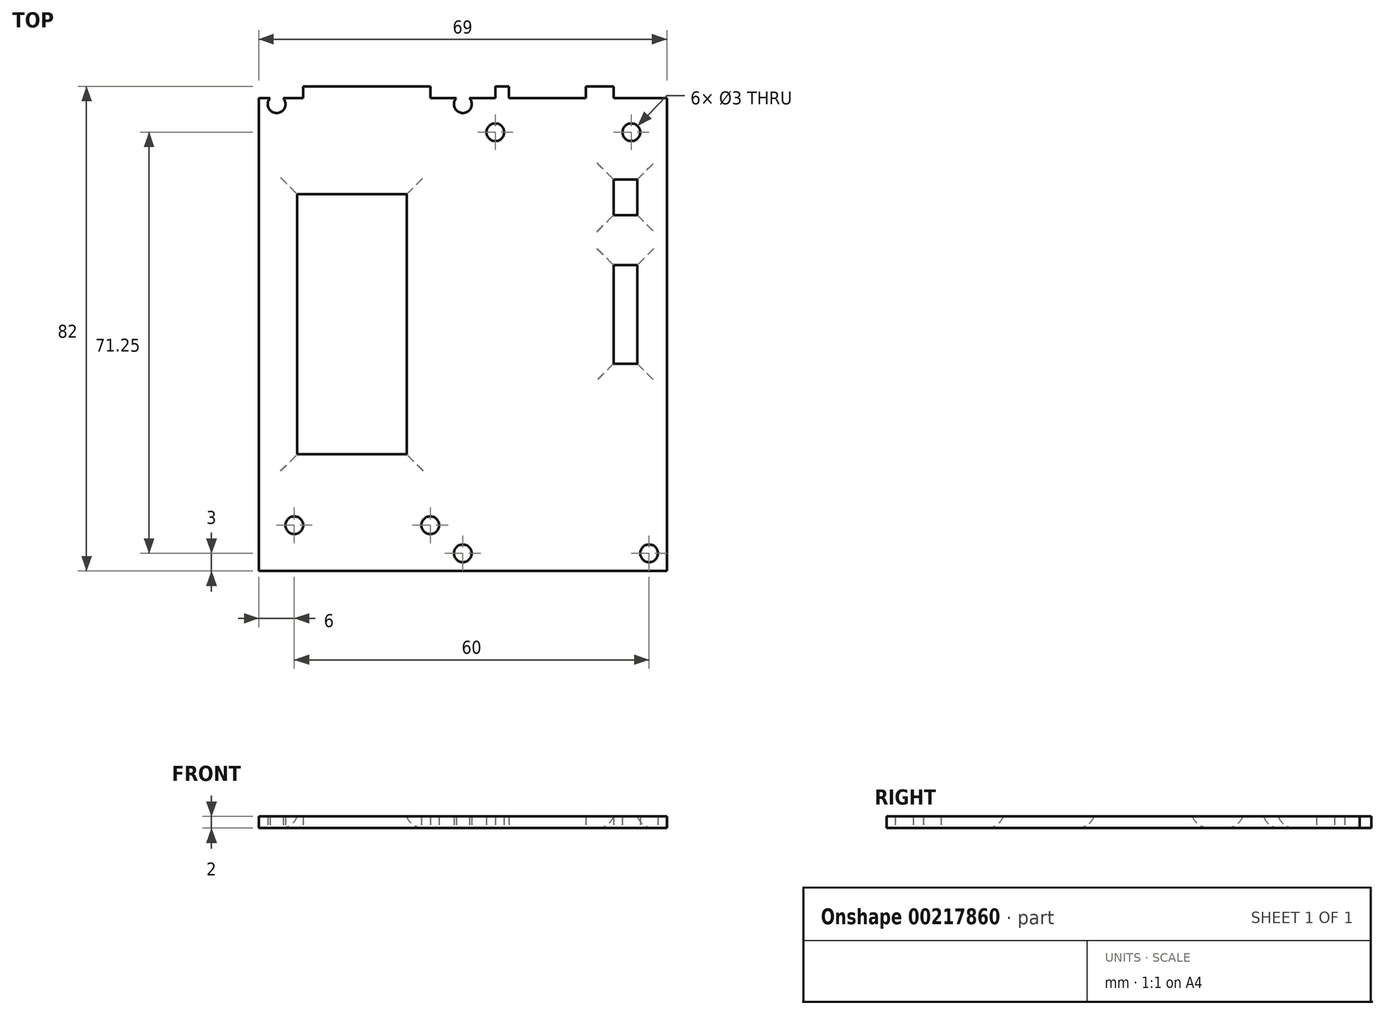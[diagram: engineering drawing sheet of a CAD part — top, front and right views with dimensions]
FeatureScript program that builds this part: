
annotation { "Feature Type Name" : "Feature", "Feature Type Description" : "" }
export const myFeature = defineFeature(function(context is Context, id is Id, definition is map)
    precondition{}
    {
        {
            var Q0;
            Q0=qCreatedBy(makeId("Top.planeOp"),FACE);
            var sketch = newSketch(context, id + "F0", { "sketchPlane" : qUnion([Q0])});
            skLineSegment(sketch, "E0.bottom", {"start": v(34.5, -41) * mm, "end": v(-34.5, -41) * mm});
            skLineSegment(sketch, "E0.top", {"start": v(34.5, 41) * mm, "end": v(-34.5, 41) * mm});
            skLineSegment(sketch, "E0.left", {"start": v(34.5, -41) * mm, "end": v(34.5, 41) * mm});
            skLineSegment(sketch, "E0.right", {"start": v(-34.5, -41) * mm, "end": v(-34.5, 41) * mm});
            skPoint(sketch, "E0.middle", {"position": v(0, 0) * mm});
            skLineSegment(sketch, "E1", {"start": v(-34.5, 39) * mm, "end": v(34.5, 39) * mm});
            skCircle(sketch, "E2.MirrorC", {"center": v(31.5, -38) * mm, "radius": 1.5 * mm});
            skCircle(sketch, "E3", {"center": v(0, -38) * mm, "radius": 1.5 * mm});
            skCircle(sketch, "E4", {"center": v(-28.5, 33.25) * mm, "radius": 1.5 * mm});
            skCircle(sketch, "E5", {"center": v(-5.5, 33.25) * mm, "radius": 1.5 * mm});
            skCircle(sketch, "E6.MirrorC", {"center": v(5.5, 33.25) * mm, "radius": 1.5 * mm});
            skCircle(sketch, "E7.MirrorC", {"center": v(28.5, 33.25) * mm, "radius": 1.5 * mm});
            skLineSegment(sketch, "E8.bottom", {"start": v(-28, 22.75) * mm, "end": v(-9.5, 22.75) * mm});
            skLineSegment(sketch, "E8.top", {"start": v(-28, -21.25) * mm, "end": v(-9.5, -21.25) * mm});
            skLineSegment(sketch, "E8.left", {"start": v(-28, 22.75) * mm, "end": v(-28, -21.25) * mm});
            skLineSegment(sketch, "E8.right", {"start": v(-9.5, 22.75) * mm, "end": v(-9.5, -21.25) * mm});
            skLineSegment(sketch, "E9.bottom", {"start": v(25.5, 25.25) * mm, "end": v(29.5, 25.25) * mm});
            skLineSegment(sketch, "E9.top", {"start": v(25.5, 19.25) * mm, "end": v(29.5, 19.25) * mm});
            skLineSegment(sketch, "E9.left", {"start": v(25.5, 25.25) * mm, "end": v(25.5, 19.25) * mm});
            skLineSegment(sketch, "E9.right", {"start": v(29.5, 25.25) * mm, "end": v(29.5, 19.25) * mm});
            skLineSegment(sketch, "E10.bottom", {"start": v(29.5, 10.75) * mm, "end": v(25.5, 10.75) * mm});
            skLineSegment(sketch, "E10.top", {"start": v(29.5, -5.91) * mm, "end": v(25.5, -5.91) * mm});
            skLineSegment(sketch, "E10.left", {"start": v(29.5, 10.75) * mm, "end": v(29.5, -5.91) * mm});
            skLineSegment(sketch, "E10.right", {"start": v(25.5, 10.75) * mm, "end": v(25.5, -5.91) * mm});
            skLineSegment(sketch, "E11.bottom", {"start": v(-5.5, 41) * mm, "end": v(5.5, 41) * mm});
            skLineSegment(sketch, "E11.top", {"start": v(-5.5, 39) * mm, "end": v(5.5, 39) * mm});
            skLineSegment(sketch, "E11.left", {"start": v(-5.5, 41) * mm, "end": v(-5.5, 39) * mm});
            skLineSegment(sketch, "E11.right", {"start": v(5.5, 41) * mm, "end": v(5.5, 39) * mm});
            skLineSegment(sketch, "E12.bottom", {"start": v(28.5, 39) * mm, "end": v(34.5, 39) * mm});
            skLineSegment(sketch, "E12.top", {"start": v(28, 41) * mm, "end": v(34.5, 41) * mm});
            skLineSegment(sketch, "E12.right", {"start": v(34.5, 39) * mm, "end": v(34.5, 41) * mm});
            skLineSegment(sketch, "E13.bottom", {"start": v(-28.5, 39) * mm, "end": v(-34.5, 39) * mm});
            skLineSegment(sketch, "E13.top", {"start": v(-27, 41) * mm, "end": v(-34.5, 41) * mm});
            skLineSegment(sketch, "E13.right", {"start": v(-34.5, 39) * mm, "end": v(-34.5, 41) * mm});
            skLineSegment(sketch, "E14", {"start": v(-25.5, 41) * mm, "end": v(-25.5, 39) * mm});
            skLineSegment(sketch, "E15.MirrorCS", {"start": v(25.5, 41) * mm, "end": v(25.5, 39) * mm});
            skLineSegment(sketch, "E16.bottom", {"start": v(-37, 41) * mm, "end": v(37, 41) * mm});
            skLineSegment(sketch, "E16.top", {"start": v(-37, -43.29) * mm, "end": v(37, -43.29) * mm});
            skLineSegment(sketch, "E16.left", {"start": v(-37, 41) * mm, "end": v(-37, -43.29) * mm});
            skLineSegment(sketch, "E16.right", {"start": v(37, 41) * mm, "end": v(37, -43.29) * mm});
            skLineSegment(sketch, "E17.bottom", {"start": v(-10.5, -43.29) * mm, "end": v(10.5, -43.29) * mm});
            skLineSegment(sketch, "E17.top", {"start": v(-10.5, -51.29) * mm, "end": v(10.5, -51.29) * mm});
            skLineSegment(sketch, "E17.left", {"start": v(-10.5, -43.29) * mm, "end": v(-10.5, -51.29) * mm});
            skLineSegment(sketch, "E17.right", {"start": v(10.5, -43.29) * mm, "end": v(10.5, -51.29) * mm});
            skLineSegment(sketch, "E18.bottom", {"start": v(-12.5, -41) * mm, "end": v(12.5, -41) * mm});
            skLineSegment(sketch, "E18.top", {"start": v(-12.5, -53.5) * mm, "end": v(12.5, -53.5) * mm});
            skLineSegment(sketch, "E18.left", {"start": v(-12.5, -41) * mm, "end": v(-12.5, -53.5) * mm});
            skLineSegment(sketch, "E18.right", {"start": v(12.5, -41) * mm, "end": v(12.5, -53.5) * mm});
            skLineSegment(sketch, "E19", {"start": v(-10.5, -43.29) * mm, "end": v(-10.5, -41) * mm});
            skLineSegment(sketch, "E20.MirrorCS", {"start": v(10.5, -43.29) * mm, "end": v(10.5, -41) * mm});
            skLineSegment(sketch, "E21.bottom", {"start": v(20.8, 41) * mm, "end": v(7.8, 41) * mm});
            skLineSegment(sketch, "E21.top", {"start": v(20.8, 39) * mm, "end": v(7.8, 39) * mm});
            skLineSegment(sketch, "E21.left", {"start": v(20.8, 41) * mm, "end": v(20.8, 39) * mm});
            skLineSegment(sketch, "E21.right", {"start": v(7.8, 41) * mm, "end": v(7.8, 39) * mm});
            skLineSegment(sketch, "E22", {"start": v(-14.5, 41) * mm, "end": v(-14.5, 39) * mm});
            skLineSegment(sketch, "E23", {"start": v(-27, 41) * mm, "end": v(-27, 39) * mm});
            skLineSegment(sketch, "E24.top", {"start": v(-37, 43) * mm, "end": v(37, 43) * mm});
            skLineSegment(sketch, "E24.left", {"start": v(-37, 41) * mm, "end": v(-37, 43) * mm});
            skLineSegment(sketch, "E24.right", {"start": v(37, 41) * mm, "end": v(37, 43) * mm});
            skCircle(sketch, "E25.MirrorC", {"center": v(-31.5, 38) * mm, "radius": 1.5 * mm});
            skCircle(sketch, "E26", {"center": v(-28.5, -33.25) * mm, "radius": 1.5 * mm});
            skCircle(sketch, "E27", {"center": v(-5.5, -33.25) * mm, "radius": 1.5 * mm});
            skCircle(sketch, "E28.MirrorC", {"center": v(0, 38) * mm, "radius": 1.5 * mm});
            skSolve(sketch);
        }
        {
            var Q0;
            {var subQ2=sQuery(id+"F0.wireOp",EDGE,"E0.bottom");Q0=makeQuery(id+"F0.imprint","IMPRINT",FACE,{"disambiguationData":[TD([[makeQuery(id+"F0.imprint","IMPRINT",EDGE,{"derivedFrom":subQ2}),-1.0]])]});}
            var Q1;
            {var subQ2=sQuery(id+"F0.wireOp",EDGE,"E13.bottom");Q1=makeQuery(id+"F0.imprint","IMPRINT",FACE,{"disambiguationData":[TD([[makeQuery(id+"F0.imprint","IMPRINT",EDGE,{"derivedFrom":subQ2}),-1.0]])]});}
            var Q2;
            {var subQ0=sQuery(id+"F0.wireOp",EDGE,"E14");Q2=makeQuery(id+"F0.imprint","IMPRINT",FACE,{"disambiguationData":[TD([[makeQuery(id+"F0.imprint","IMPRINT",EDGE,{"derivedFrom":subQ0}),-1.0]])]});}
            var Q3;
            {var subQ0=sQuery(id+"F0.wireOp",EDGE,"E14");Q3=makeQuery(id+"F0.imprint","IMPRINT",FACE,{"disambiguationData":[TD([[makeQuery(id+"F0.imprint","IMPRINT",EDGE,{"derivedFrom":subQ0}),1.0]])]});}
            var Q4;
            {var subQ0=sQuery(id+"F0.wireOp",EDGE,"E11.left");Q4=makeQuery(id+"F0.imprint","IMPRINT",FACE,{"disambiguationData":[TD([[makeQuery(id+"F0.imprint","IMPRINT",EDGE,{"derivedFrom":subQ0}),-1.0]])]});}
            var Q5;
            Q5=makeQuery(id+"F0.imprint","IMPRINT",FACE,{"disambiguationData":[TD([[makeQuery(id+"F0.imprint","IMPRINT",EDGE,{"derivedFrom":sQuery(id+"F0.wireOp",EDGE,"E11.top")}),1.0]])]});
            var Q6;
            {var subQ0=sQuery(id+"F0.wireOp",EDGE,"E11.right");Q6=makeQuery(id+"F0.imprint","IMPRINT",FACE,{"disambiguationData":[TD([[makeQuery(id+"F0.imprint","IMPRINT",EDGE,{"derivedFrom":subQ0}),1.0]])]});}
            var Q7;
            Q7=makeQuery(id+"F0.imprint","IMPRINT",FACE,{"disambiguationData":[TD([[makeQuery(id+"F0.imprint","IMPRINT",EDGE,{"derivedFrom":sQuery(id+"F0.wireOp",EDGE,"E21.top")}),-1.0]])]});
            var Q8;
            {var subQ0=sQuery(id+"F0.wireOp",EDGE,"E15.MirrorCS");Q8=makeQuery(id+"F0.imprint","IMPRINT",FACE,{"disambiguationData":[TD([[makeQuery(id+"F0.imprint","IMPRINT",EDGE,{"derivedFrom":subQ0}),-1.0]])]});}
            var Q9;
            {var subQ2=sQuery(id+"F0.wireOp",EDGE,"E12.bottom");Q9=makeQuery(id+"F0.imprint","IMPRINT",FACE,{"disambiguationData":[TD([[makeQuery(id+"F0.imprint","IMPRINT",EDGE,{"derivedFrom":subQ2}),1.0]])]});}
            var Q10;
            Q10=makeQuery(id+"F0.imprint","IMPRINT",FACE,{"disambiguationData":[TD([[makeQuery(id+"F0.imprint","IMPRINT",EDGE,{"derivedFrom":sQuery(id+"F0.wireOp",EDGE,"E5")}),1.0]])]});
            var Q11;
            Q11=makeQuery(id+"F0.imprint","IMPRINT",FACE,{"disambiguationData":[TD([[makeQuery(id+"F0.imprint","IMPRINT",EDGE,{"derivedFrom":sQuery(id+"F0.wireOp",EDGE,"E4")}),1.0]])]});
            extrude(context, id + "F1", {"entities" : qUnion([Q0, Q1, Q2, Q3, Q4, Q5, Q6, Q7, Q8, Q9, Q10, Q11]), "depth" : 2 * mm});
        }
        {
            var Q0;
            Q0=makeQuery(id+"F1.opExtrude","CAP_EDGE",EDGE,{"disambiguationData":[OSD([sQuery(id+"F0.wireOp",EDGE,"E10.right")])],"isStart":true});
            var Q1;
            Q1=makeQuery(id+"F1.opExtrude","CAP_EDGE",EDGE,{"disambiguationData":[OSD([sQuery(id+"F0.wireOp",EDGE,"E10.top")])],"isStart":true});
            var Q2;
            Q2=makeQuery(id+"F1.opExtrude","CAP_EDGE",EDGE,{"disambiguationData":[OSD([sQuery(id+"F0.wireOp",EDGE,"E10.left")])],"isStart":true});
            var Q3;
            Q3=makeQuery(id+"F1.opExtrude","CAP_EDGE",EDGE,{"disambiguationData":[OSD([sQuery(id+"F0.wireOp",EDGE,"E10.bottom")])],"isStart":true});
            var Q4;
            Q4=makeQuery(id+"F1.opExtrude","CAP_EDGE",EDGE,{"disambiguationData":[OSD([sQuery(id+"F0.wireOp",EDGE,"E9.top")])],"isStart":true});
            var Q5;
            Q5=makeQuery(id+"F1.opExtrude","CAP_EDGE",EDGE,{"disambiguationData":[OSD([sQuery(id+"F0.wireOp",EDGE,"E9.right")])],"isStart":true});
            var Q6;
            Q6=makeQuery(id+"F1.opExtrude","CAP_EDGE",EDGE,{"disambiguationData":[OSD([sQuery(id+"F0.wireOp",EDGE,"E9.bottom")])],"isStart":true});
            var Q7;
            Q7=makeQuery(id+"F1.opExtrude","CAP_EDGE",EDGE,{"disambiguationData":[OSD([sQuery(id+"F0.wireOp",EDGE,"E9.left")])],"isStart":true});
            var Q8;
            Q8=makeQuery(id+"F1.opExtrude","CAP_EDGE",EDGE,{"disambiguationData":[OSD([sQuery(id+"F0.wireOp",EDGE,"E8.right")])],"isStart":true});
            var Q9;
            Q9=makeQuery(id+"F1.opExtrude","CAP_EDGE",EDGE,{"disambiguationData":[OSD([sQuery(id+"F0.wireOp",EDGE,"E8.top")])],"isStart":true});
            var Q10;
            Q10=makeQuery(id+"F1.opExtrude","CAP_EDGE",EDGE,{"disambiguationData":[OSD([sQuery(id+"F0.wireOp",EDGE,"E8.bottom")])],"isStart":true});
            var Q11;
            Q11=makeQuery(id+"F1.opExtrude","CAP_EDGE",EDGE,{"disambiguationData":[OSD([sQuery(id+"F0.wireOp",EDGE,"E8.left")])],"isStart":true});
            fillet(context, id + "F2", {"entities" : qUnion([Q0, Q1, Q2, Q3, Q4, Q5, Q6, Q7, Q8, Q9, Q10, Q11]), "radius" : 3 * mm, "tangentPropagation" : true, "allowEdgeOverflow" : false});
        }
    });
